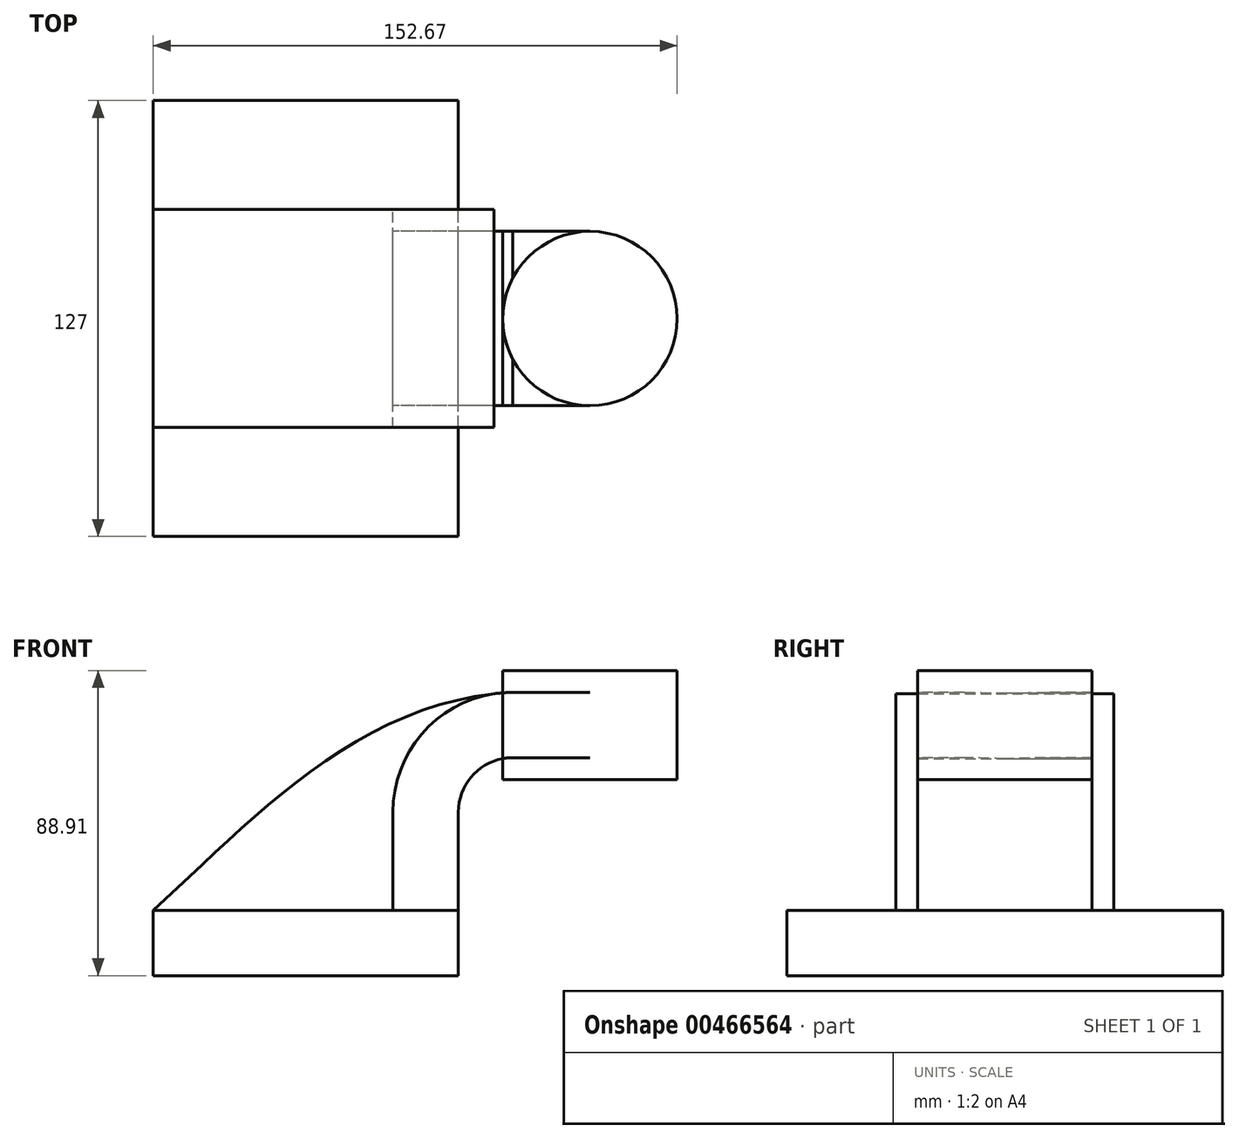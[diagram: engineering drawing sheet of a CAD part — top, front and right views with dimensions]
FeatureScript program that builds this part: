
annotation { "Feature Type Name" : "Feature", "Feature Type Description" : "" }
export const myFeature = defineFeature(function(context is Context, id is Id, definition is map)
    precondition{}
    {
        {
            var Q0;
            Q0=qCreatedBy(makeId("Front.planeOp"),FACE);
            var sketch = newSketch(context, id + "F0", { "sketchPlane" : qUnion([Q0])});
            skLineSegment(sketch, "E0.bottom", {"start": v(44.45, 9.53) * mm, "end": v(-44.45, 9.53) * mm});
            skLineSegment(sketch, "E0.top", {"start": v(44.45, -9.52) * mm, "end": v(-44.45, -9.52) * mm});
            skLineSegment(sketch, "E0.left", {"start": v(44.45, 9.53) * mm, "end": v(44.45, -9.52) * mm});
            skLineSegment(sketch, "E0.right", {"start": v(-44.45, 9.53) * mm, "end": v(-44.45, -9.52) * mm});
            skPoint(sketch, "E0.middle", {"position": v(0, 0) * mm});
            skLineSegment(sketch, "E1.bottom", {"start": v(57.42, 47.63) * mm, "end": v(108.22, 47.63) * mm});
            skLineSegment(sketch, "E1.top", {"start": v(57.42, 79.38) * mm, "end": v(108.22, 79.38) * mm});
            skLineSegment(sketch, "E1.left", {"start": v(57.42, 47.63) * mm, "end": v(57.42, 79.38) * mm});
            skLineSegment(sketch, "E1.right", {"start": v(108.22, 47.63) * mm, "end": v(108.22, 79.38) * mm});
            skPoint(sketch, "E1.middle", {"position": v(82.82, 63.5) * mm});
            skLineSegment(sketch, "E2", {"start": v(44.45, 9.53) * mm, "end": v(44.45, 38.1) * mm});
            skArc(sketch, "E3", {"start": v(44.45, 38.1) * mm, "mid": v(49.1, 49.33) * mm, "end": v(60.32, 53.98) * mm});
            skLineSegment(sketch, "E4", {"start": v(60.32, 53.98) * mm, "end": v(82.82, 53.98) * mm});
            skLineSegment(sketch, "E5.0", {"start": v(60.32, 73.03) * mm, "end": v(82.82, 73.03) * mm});
            skArc(sketch, "E5.1", {"start": v(25.4, 38.1) * mm, "mid": v(35.63, 62.8) * mm, "end": v(60.32, 73.03) * mm});
            skLineSegment(sketch, "E5.2", {"start": v(25.4, 9.53) * mm, "end": v(25.4, 38.1) * mm});
            skLineSegment(sketch, "E6", {"start": v(82.82, 79.38) * mm, "end": v(82.82, 47.63) * mm});
            skFitSpline(sketch, "E7", {"points": [v(-44.45, 9.53) * mm, v(60.33, 73.03) * mm], "startDerivative": vector(83.86, 75.75) * mm, "endDerivative": vector(135.5, 6.42) * mm});
            skSolve(sketch);
        }
        {
            var Q0;
            Q0=makeQuery(id+"F0.imprint","IMPRINT",FACE,{"disambiguationData":[TD([[makeQuery(id+"F0.imprint","IMPRINT",EDGE,{"derivedFrom":sQuery(id+"F0.wireOp",EDGE,"E0.top")}),-1.0]])]});
            extrude(context, id + "F1", {"entities" : qUnion([Q0]), "endBound" : BoundingType.SYMMETRIC, "depth" : 127 * mm});
        }
        {
            var Q0;
            {var subQ3=sQuery(id+"F0.wireOp",EDGE,"E5.2");Q0=makeQuery(id+"F0.imprint","IMPRINT",FACE,{"disambiguationData":[TD([[makeQuery(id+"F0.imprint","IMPRINT",EDGE,{"derivedFrom":subQ3}),1.0]])]});}
            extrude(context, id + "F2", {"entities" : qUnion([Q0]), "operationType" : NewBodyOperationType.ADD, "endBound" : BoundingType.SYMMETRIC, "depth" : 63.5 * mm});
        }
        {
            var Q0;
            {var subQ1=sQuery(id+"F0.wireOp",EDGE,"E4");Q0=makeQuery(id+"F0.imprint","IMPRINT",FACE,{"disambiguationData":[TD([[makeQuery(id+"F0.imprint","IMPRINT",EDGE,{"derivedFrom":subQ1}),1.0]])]});}
            extrude(context, id + "F3", {"entities" : qUnion([Q0]), "operationType" : NewBodyOperationType.ADD, "endBound" : BoundingType.SYMMETRIC, "depth" : 50.8 * mm});
        }
        {
            var Q0;
            {var subQ4=sQuery(id+"F0.wireOp",EDGE,"E1.right");Q0=makeQuery(id+"F0.imprint","IMPRINT",FACE,{"disambiguationData":[TD([[makeQuery(id+"F0.imprint","IMPRINT",EDGE,{"derivedFrom":subQ4}),1.0]])]});}
            var Q1;
            Q1=sQuery(id+"F0.wireOp",EDGE,"E6");
            revolve(context, id + "F4", {"operationType" : NewBodyOperationType.ADD, "entities" : qUnion([Q0]), "axis" : qUnion([Q1]), "revolveType" : RevolveType.FULL});
        }
        {
            var Q0;
            {var subQ0=sQuery(id+"F0.wireOp",EDGE,"E2");Q0=makeQuery(id+"F0.imprint","IMPRINT",FACE,{"disambiguationData":[TD([[makeQuery(id+"F0.imprint","IMPRINT",EDGE,{"derivedFrom":subQ0}),1.0]])]});}
            extrude(context, id + "F5", {"entities" : qUnion([Q0]), "endBound" : BoundingType.SYMMETRIC, "depth" : 50.8 * mm});
        }
    });
